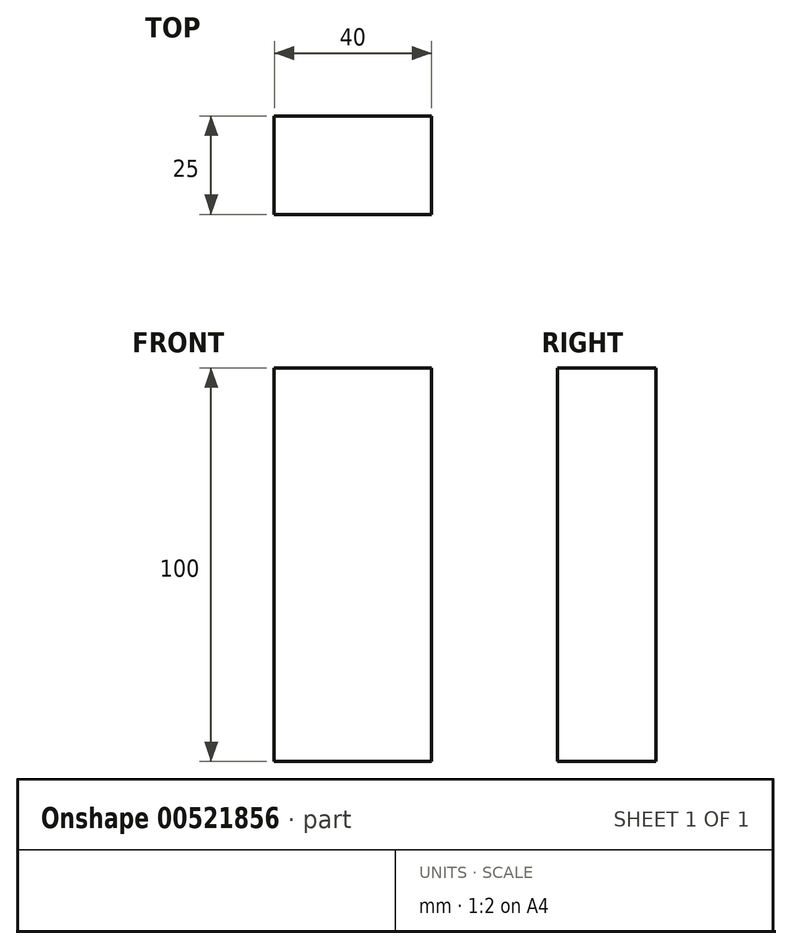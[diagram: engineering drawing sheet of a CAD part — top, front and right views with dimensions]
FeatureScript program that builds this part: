
annotation { "Feature Type Name" : "Feature", "Feature Type Description" : "" }
export const myFeature = defineFeature(function(context is Context, id is Id, definition is map)
    precondition{}
    {
        {
            var Q0;
            Q0=qCreatedBy(makeId("Front.planeOp"),FACE);
            var sketch = newSketch(context, id + "F0", { "sketchPlane" : qUnion([Q0])});
            skLineSegment(sketch, "E0.bottom", {"start": v(-21.1, -27.8) * mm, "end": v(18.9, -27.8) * mm});
            skLineSegment(sketch, "E0.top", {"start": v(-21.1, 72.2) * mm, "end": v(18.9, 72.2) * mm});
            skLineSegment(sketch, "E0.left", {"start": v(-21.1, -27.8) * mm, "end": v(-21.1, 72.2) * mm});
            skLineSegment(sketch, "E0.right", {"start": v(18.9, -27.8) * mm, "end": v(18.9, 72.2) * mm});
            skSolve(sketch);
        }
        {
            var Q0;
            Q0=makeQuery(id+"F0.imprint","IMPRINT",FACE,{"disambiguationData":[TD([[makeQuery(id+"F0.imprint","IMPRINT",EDGE,{"derivedFrom":sQuery(id+"F0.wireOp",EDGE,"E0.bottom")}),1.0]])]});
            extrude(context, id + "F1", {"entities" : qUnion([Q0]), "depth" : 25 * mm, "offsetDistance" : 25 * mm});
        }
    });
